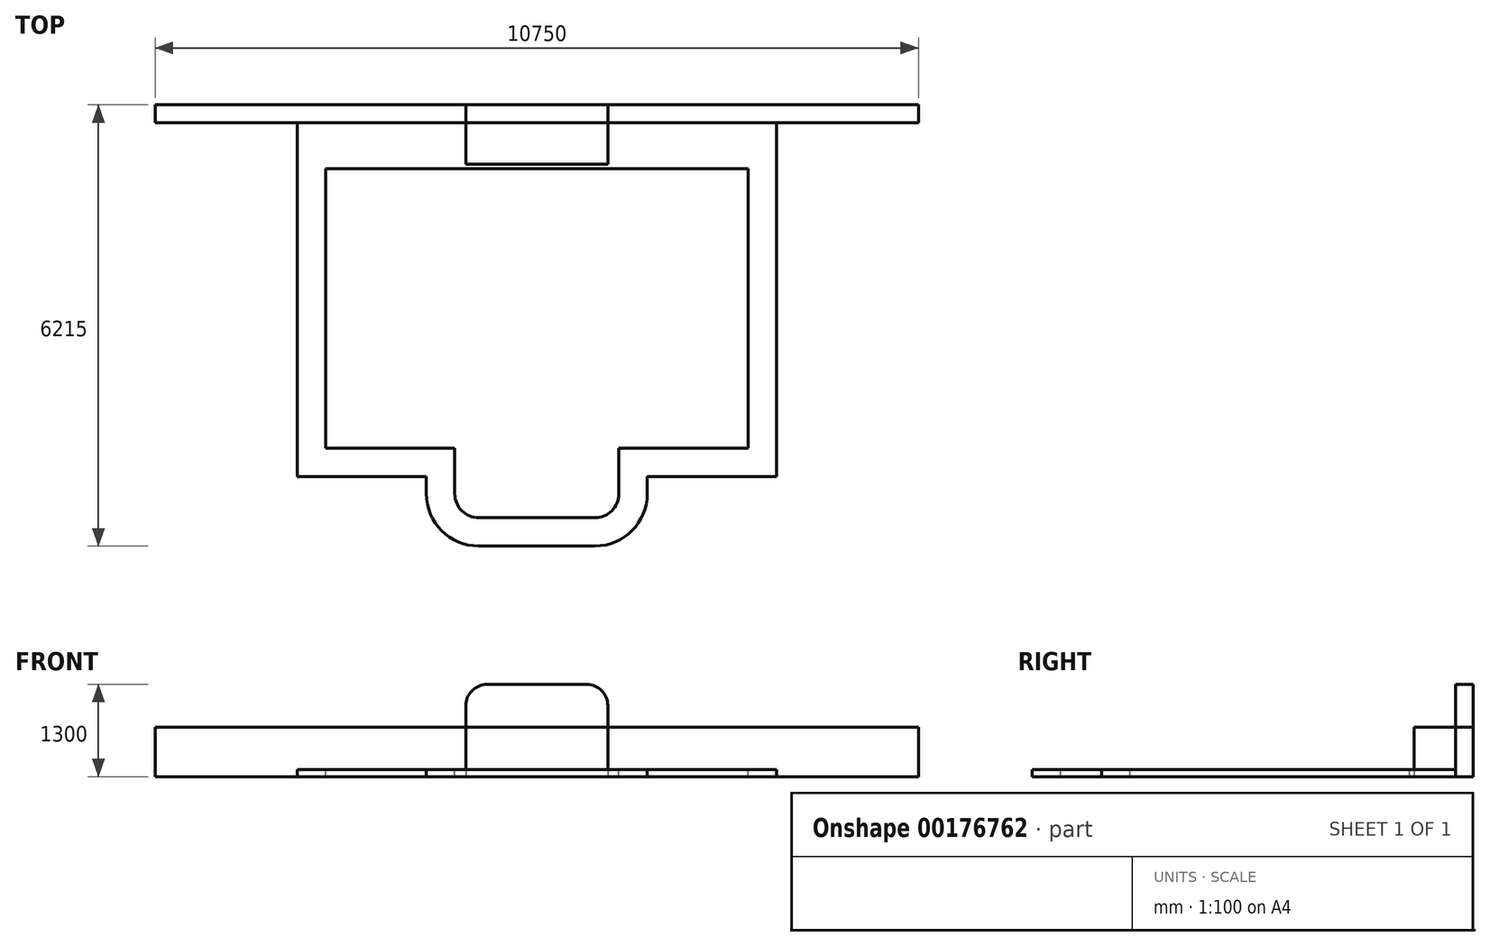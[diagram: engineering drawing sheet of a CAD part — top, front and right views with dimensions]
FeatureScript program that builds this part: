
annotation { "Feature Type Name" : "Feature", "Feature Type Description" : "" }
export const myFeature = defineFeature(function(context is Context, id is Id, definition is map)
    precondition{}
    {
        {
            var Q0;
            Q0=qCreatedBy(makeId("Top.planeOp"),FACE);
            var sketch = newSketch(context, id + "F0", { "sketchPlane" : qUnion([Q0])});
            skLineSegment(sketch, "E0.bottom", {"start": v(-3375, 0) * mm, "end": v(3375, 0) * mm});
            skLineSegment(sketch, "E0.top", {"start": v(-3375, -4985) * mm, "end": v(-1555, -4985) * mm});
            skLineSegment(sketch, "E0.left", {"start": v(-3375, 0) * mm, "end": v(-3375, -4985) * mm});
            skLineSegment(sketch, "E0.right", {"start": v(3375, 0) * mm, "end": v(3375, -4985) * mm});
            skLineSegment(sketch, "E1", {"start": v(-1000, 0) * mm, "end": v(-1000, -585) * mm});
            skLineSegment(sketch, "E2", {"start": v(-1000, -585) * mm, "end": v(1000, -585) * mm});
            skLineSegment(sketch, "E3", {"start": v(1000, -585) * mm, "end": v(1000, 0) * mm});
            skLineSegment(sketch, "E4.bottom", {"start": v(-2975, -650) * mm, "end": v(2975, -650) * mm});
            skLineSegment(sketch, "E4.top", {"start": v(-2975, -4585) * mm, "end": v(-1155, -4585) * mm});
            skLineSegment(sketch, "E4.left", {"start": v(-2975, -650) * mm, "end": v(-2975, -4585) * mm});
            skLineSegment(sketch, "E4.right", {"start": v(2975, -650) * mm, "end": v(2975, -4585) * mm});
            skLineSegment(sketch, "E5", {"start": v(-1555, -4985) * mm, "end": v(-1555, -5230) * mm});
            skLineSegment(sketch, "E6", {"start": v(-820, -5965) * mm, "end": v(820, -5965) * mm});
            skLineSegment(sketch, "E7", {"start": v(1555, -5230) * mm, "end": v(1555, -4985) * mm});
            skLineSegment(sketch, "E8.trimOffspring", {"start": v(1555, -4985) * mm, "end": v(3375, -4985) * mm});
            skPoint(sketch, "E9.visualSharp", {"position": v(-1555, -5965) * mm});
            skArc(sketch, "E9.filletArc", {"start": v(-1555, -5230) * mm, "mid": v(-1339.72, -5749.72) * mm, "end": v(-820, -5965) * mm});
            skPoint(sketch, "E10.visualSharp", {"position": v(1555, -5965) * mm});
            skArc(sketch, "E10.filletArc", {"start": v(820, -5965) * mm, "mid": v(1339.72, -5749.72) * mm, "end": v(1555, -5230) * mm});
            skLineSegment(sketch, "E11.0", {"start": v(1155, -5230) * mm, "end": v(1155, -4585) * mm});
            skLineSegment(sketch, "E11.1", {"start": v(-1155, -4585) * mm, "end": v(-1155, -5230) * mm});
            skArc(sketch, "E11.2", {"start": v(-1155, -5230) * mm, "mid": v(-1056.88, -5466.88) * mm, "end": v(-820, -5565) * mm});
            skLineSegment(sketch, "E11.3", {"start": v(-820, -5565) * mm, "end": v(820, -5565) * mm});
            skArc(sketch, "E11.4", {"start": v(820, -5565) * mm, "mid": v(1056.88, -5466.88) * mm, "end": v(1155, -5230) * mm});
            skLineSegment(sketch, "E12", {"start": v(-1155, -4585) * mm, "end": v(-1155, -4585) * mm});
            skLineSegment(sketch, "E13", {"start": v(1155, -4585) * mm, "end": v(1155, -4585) * mm});
            skLineSegment(sketch, "E14.trimOffspring", {"start": v(1155, -4585) * mm, "end": v(2975, -4585) * mm});
            skLineSegment(sketch, "E15.bottom", {"start": v(-5375, 0) * mm, "end": v(5375, 0) * mm});
            skLineSegment(sketch, "E15.top", {"start": v(-5375, 250) * mm, "end": v(5375, 250) * mm});
            skLineSegment(sketch, "E15.left", {"start": v(-5375, 0) * mm, "end": v(-5375, 250) * mm});
            skLineSegment(sketch, "E15.right", {"start": v(5375, 0) * mm, "end": v(5375, 250) * mm});
            skLineSegment(sketch, "E16", {"start": v(-1000, 0) * mm, "end": v(-1000, 250) * mm});
            skLineSegment(sketch, "E17", {"start": v(1000, 0) * mm, "end": v(1000, 250) * mm});
            skSolve(sketch);
        }
        {
            var Q0;
            Q0=makeQuery(id+"F0.imprint","IMPRINT",FACE,{"disambiguationData":[TD([[makeQuery(id+"F0.imprint","IMPRINT",EDGE,{"derivedFrom":sQuery(id+"F0.wireOp",EDGE,"E0.top")}),1.0]])]});
            extrude(context, id + "F1", {"entities" : qUnion([Q0]), "oppositeDirection" : true, "depth" : 100 * mm});
        }
        {
            var Q0;
            Q0=makeQuery(id+"F0.imprint","IMPRINT",FACE,{"disambiguationData":[TD([[makeQuery(id+"F0.imprint","IMPRINT",EDGE,{"derivedFrom":sQuery(id+"F0.wireOp",EDGE,"E15.top")}),-1.0]])]});
            extrude(context, id + "F2", {"entities" : qUnion([Q0]), "operationType" : NewBodyOperationType.ADD, "depth" : 1200 * mm, "hasSecondDirection" : true, "secondDirectionOppositeDirection" : true, "secondDirectionDepth" : 100 * mm});
        }
        {
            var Q0;
            {var subQ0=sQuery(id+"F0.wireOp",EDGE,"E15.left");Q0=makeQuery(id+"F0.imprint","IMPRINT",FACE,{"disambiguationData":[TD([[makeQuery(id+"F0.imprint","IMPRINT",EDGE,{"derivedFrom":subQ0}),-1.0]])]});}
            var Q1;
            {var subQ0=sQuery(id+"F0.wireOp",EDGE,"E15.right");Q1=makeQuery(id+"F0.imprint","IMPRINT",FACE,{"disambiguationData":[TD([[makeQuery(id+"F0.imprint","IMPRINT",EDGE,{"derivedFrom":subQ0}),1.0]])]});}
            extrude(context, id + "F3", {"entities" : qUnion([Q0, Q1]), "depth" : 600 * mm, "hasSecondDirection" : true, "secondDirectionOppositeDirection" : true, "secondDirectionDepth" : 100 * mm});
        }
        {
            var Q0;
            {var subQ0=sQuery(id+"F0.wireOp",EDGE,"E1");Q0=makeQuery(id+"F0.imprint","IMPRINT",FACE,{"disambiguationData":[TD([[makeQuery(id+"F0.imprint","IMPRINT",EDGE,{"derivedFrom":subQ0}),1.0]])]});}
            extrude(context, id + "F4", {"entities" : qUnion([Q0]), "depth" : 600 * mm, "hasSecondDirection" : true, "secondDirectionOppositeDirection" : true, "secondDirectionDepth" : 100 * mm});
        }
        {
            var Q0;
            Q0=makeQuery(id+"F2.opExtrude","CAP_EDGE",EDGE,{"disambiguationData":[OSD([sQuery(id+"F0.wireOp",EDGE,"E16")])],"isStart":false});
            var Q1;
            Q1=makeQuery(id+"F2.opExtrude","CAP_EDGE",EDGE,{"disambiguationData":[OSD([sQuery(id+"F0.wireOp",EDGE,"E17")])],"isStart":false});
            fillet(context, id + "F5", {"entities" : qUnion([Q0, Q1]), "radius" : 300 * mm, "tangentPropagation" : true, "allowEdgeOverflow" : false});
        }
    });
